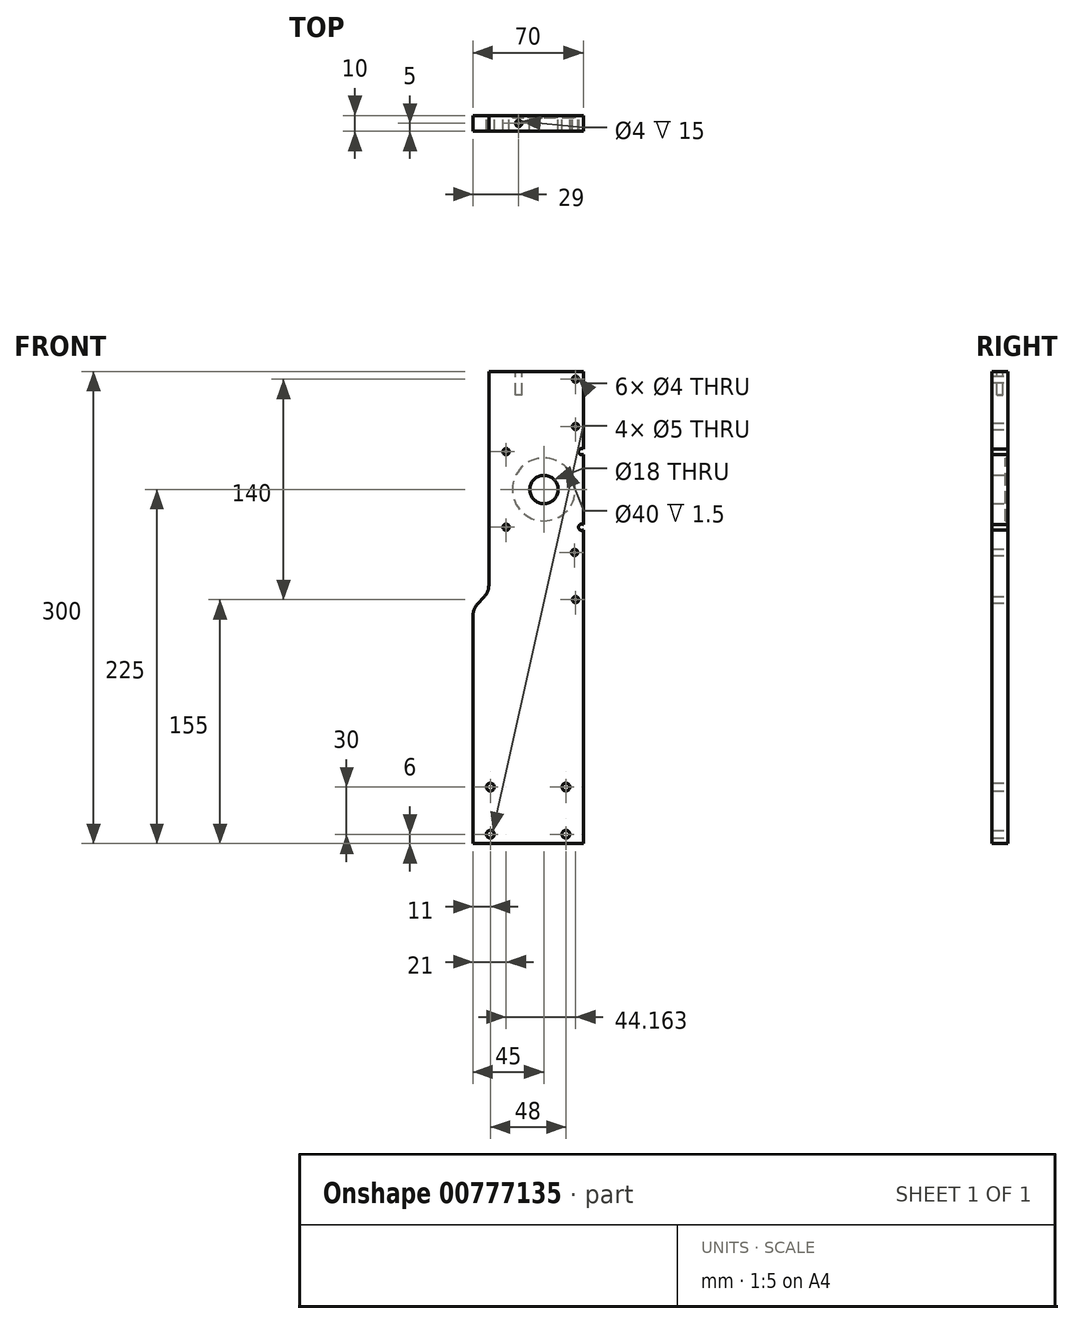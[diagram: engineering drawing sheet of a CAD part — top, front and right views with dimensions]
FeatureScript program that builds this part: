
annotation { "Feature Type Name" : "Feature", "Feature Type Description" : "" }
export const myFeature = defineFeature(function(context is Context, id is Id, definition is map)
    precondition{}
    {
        {
            var Q0;
            Q0=qCreatedBy(makeId("Front.planeOp"),FACE);
            var sketch = newSketch(context, id + "F0", { "sketchPlane" : qUnion([Q0])});
            skLineSegment(sketch, "E0.bottom", {"start": v(0, 0) * mm, "end": v(-70, 0) * mm});
            skLineSegment(sketch, "E0.top", {"start": v(0, 300) * mm, "end": v(-70, 300) * mm});
            skLineSegment(sketch, "E0.left", {"start": v(0, 0) * mm, "end": v(0, 300) * mm});
            skLineSegment(sketch, "E0.right", {"start": v(-70, 0) * mm, "end": v(-70, 145.1) * mm});
            skLineSegment(sketch, "E1", {"start": v(-60, 300) * mm, "end": v(-60, 163.85) * mm});
            skLineSegment(sketch, "E2", {"start": v(-62.58, 157.14) * mm, "end": v(-67.42, 151.8) * mm});
            skPoint(sketch, "E3.visualSharp", {"position": v(-60, 160) * mm});
            skArc(sketch, "E3.filletArc", {"start": v(-62.58, 157.14) * mm, "mid": v(-60.67, 160.26) * mm, "end": v(-60, 163.85) * mm});
            skPoint(sketch, "E4.newPointA", {"position": v(-73.57, 145) * mm});
            skArc(sketch, "E4.filletArc", {"start": v(-67.42, 151.8) * mm, "mid": v(-69.33, 148.69) * mm, "end": v(-70, 145.1) * mm});
            skCircle(sketch, "E5", {"center": v(-25, 225) * mm, "radius": 9 * mm});
            skCircle(sketch, "E6", {"center": v(-4.84, 295) * mm, "radius": 2 * mm});
            skCircle(sketch, "E7", {"center": v(-4.84, 265) * mm, "radius": 2 * mm});
            skCircle(sketch, "E8", {"center": v(-4.84, 155) * mm, "radius": 2 * mm});
            skCircle(sketch, "E9", {"center": v(-59, 6) * mm, "radius": 2.5 * mm});
            skCircle(sketch, "E10", {"center": v(-11, 6) * mm, "radius": 2.5 * mm});
            skCircle(sketch, "E11", {"center": v(-59, 36) * mm, "radius": 2.5 * mm});
            skCircle(sketch, "E12", {"center": v(-11, 36) * mm, "radius": 2.5 * mm});
            skCircle(sketch, "E13", {"center": v(-25, 225) * mm, "radius": 20 * mm});
            skLineSegment(sketch, "E14.bottom", {"start": v(0, 300) * mm, "end": v(5, 300) * mm});
            skLineSegment(sketch, "E14.top", {"start": v(0, 0) * mm, "end": v(5, 0) * mm});
            skLineSegment(sketch, "E14.left", {"start": v(0, 300) * mm, "end": v(0, 0) * mm});
            skLineSegment(sketch, "E14.right", {"start": v(5, 300) * mm, "end": v(5, 0) * mm});
            skCircle(sketch, "E15", {"center": v(-5.47, 185) * mm, "radius": 2 * mm});
            skCircle(sketch, "E16", {"center": v(-49, 249) * mm, "radius": 2 * mm});
            skCircle(sketch, "E17", {"center": v(-1, 249) * mm, "radius": 2 * mm});
            skCircle(sketch, "E18", {"center": v(-1, 201) * mm, "radius": 2 * mm});
            skCircle(sketch, "E19", {"center": v(-49, 201) * mm, "radius": 2 * mm});
            skSolve(sketch);
        }
        {
            var Q0;
            Q0=makeQuery(id+"F0.imprint","IMPRINT",FACE,{"disambiguationData":[TD([[makeQuery(id+"F0.imprint","IMPRINT",EDGE,{"derivedFrom":sQuery(id+"F0.wireOp",EDGE,"E0.bottom")}),-1.0]])]});
            var Q1;
            Q1=makeQuery(id+"F0.imprint","IMPRINT",FACE,{"disambiguationData":[TD([[makeQuery(id+"F0.imprint","IMPRINT",EDGE,{"derivedFrom":sQuery(id+"F0.wireOp",EDGE,"E5")}),-1.0]])]});
            var Q2;
            {var subQ5=sQuery(id+"F0.wireOp",EDGE,"E14.bottom");Q2=makeQuery(id+"F0.imprint","IMPRINT",FACE,{"disambiguationData":[TD([[makeQuery(id+"F0.imprint","IMPRINT",EDGE,{"derivedFrom":subQ5}),-1.0]])]});}
            extrude(context, id + "F1", {"entities" : qUnion([Q0, Q1, Q2]), "depth" : 10 * mm, "offsetDistance" : 25 * mm});
        }
        {
            var Q0;
            Q0=makeQuery(id+"F1.opExtrude","SWEPT_FACE",FACE,{"disambiguationData":[OSD([sQuery(id+"F0.wireOp",EDGE,"E0.top")])]});
            var sketch = newSketch(context, id + "F2", { "sketchPlane" : qUnion([Q0])});
            skCircle(sketch, "E20", {"center": v(-41, -5) * mm, "radius": 2 * mm});
            skPoint(sketch, "E20.centerSnap0", {"position": v(-27.5, 0) * mm});
            skSolve(sketch);
        }
        {
            var Q0;
            Q0=makeQuery(id+"F2.imprint","IMPRINT",FACE,{"disambiguationData":[TD([[makeQuery(id+"F2.imprint","IMPRINT",EDGE,{"derivedFrom":sQuery(id+"F2.wireOp",EDGE,"E20")}),1.0]])]});
            extrude(context, id + "F3", {"entities" : qUnion([Q0]), "operationType" : NewBodyOperationType.REMOVE, "oppositeDirection" : true, "depth" : 15 * mm, "offsetDistance" : 25 * mm});
        }
        {
            var Q0;
            Q0=makeQuery(id+"F0.imprint","IMPRINT",FACE,{"disambiguationData":[TD([[makeQuery(id+"F0.imprint","IMPRINT",EDGE,{"derivedFrom":sQuery(id+"F0.wireOp",EDGE,"E5")}),-1.0]])]});
            extrude(context, id + "F4", {"entities" : qUnion([Q0]), "operationType" : NewBodyOperationType.REMOVE, "depth" : 1.5 * mm, "offsetDistance" : 25 * mm});
        }
    });
